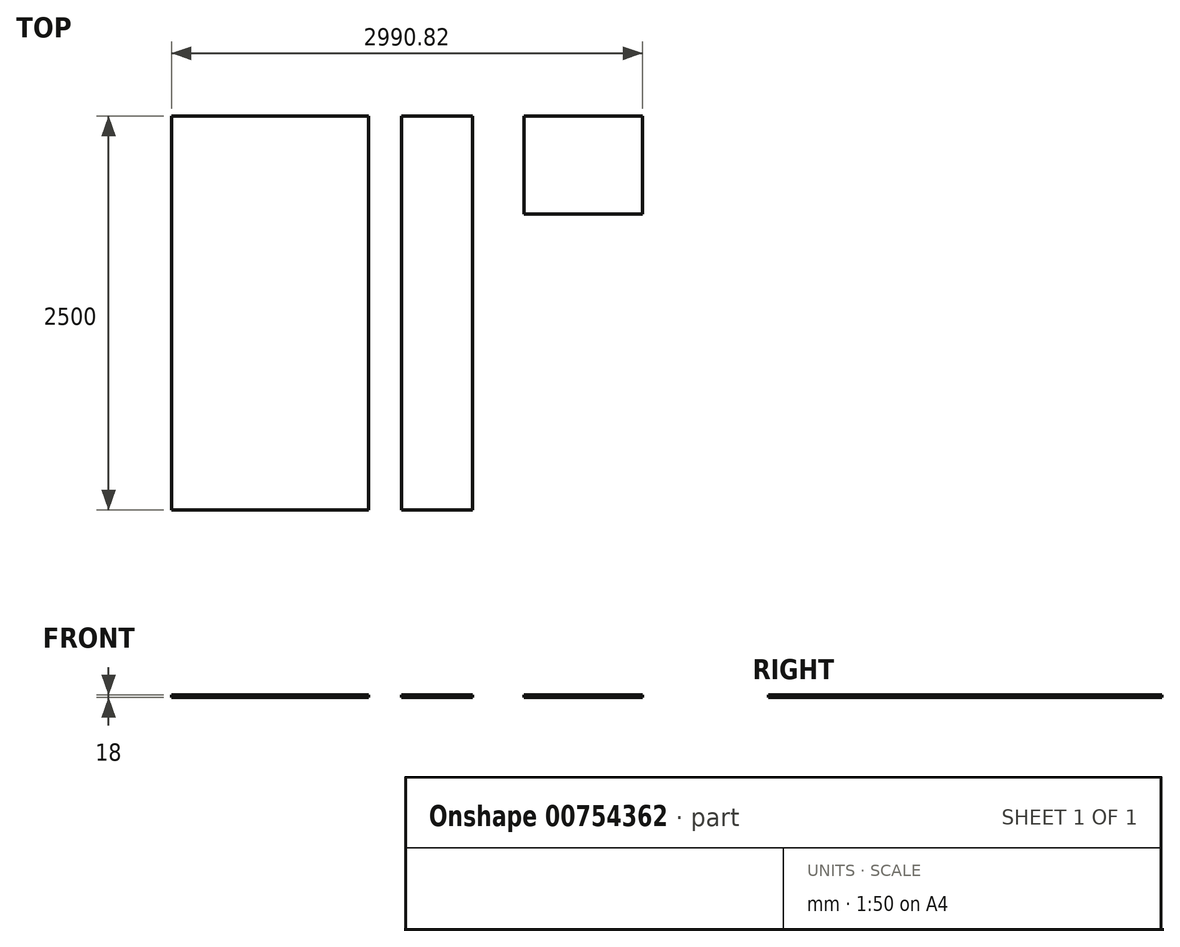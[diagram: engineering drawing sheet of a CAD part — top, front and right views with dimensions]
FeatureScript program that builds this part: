
annotation { "Feature Type Name" : "Feature", "Feature Type Description" : "" }
export const myFeature = defineFeature(function(context is Context, id is Id, definition is map)
    precondition{}
    {
        {
            var Q0;
            Q0=qCreatedBy(makeId("Top.planeOp"),FACE);
            var sketch = newSketch(context, id + "F0", { "sketchPlane" : qUnion([Q0])});
            skLineSegment(sketch, "E0.bottom", {"start": v(0, 0) * mm, "end": v(-1250, 0) * mm});
            skLineSegment(sketch, "E0.top", {"start": v(0, -2500) * mm, "end": v(-1250, -2500) * mm});
            skLineSegment(sketch, "E0.left", {"start": v(0, 0) * mm, "end": v(0, -2500) * mm});
            skLineSegment(sketch, "E0.right", {"start": v(-1250, 0) * mm, "end": v(-1250, -2500) * mm});
            skSolve(sketch);
        }
        {
            var Q0;
            Q0=makeQuery(id+"F0.imprint","IMPRINT",FACE,{"disambiguationData":[TD([[makeQuery(id+"F0.imprint","IMPRINT",EDGE,{"derivedFrom":sQuery(id+"F0.wireOp",EDGE,"E0.bottom")}),1.0]])]});
            extrude(context, id + "F1", {"entities" : qUnion([Q0]), "depth" : 18 * mm, "offsetDistance" : 25 * mm});
        }
        {
            var Q0;
            Q0=qCreatedBy(makeId("Top.planeOp"),FACE);
            var sketch = newSketch(context, id + "F2", { "sketchPlane" : qUnion([Q0])});
            skLineSegment(sketch, "E1.bottom", {"start": v(211.07, 0) * mm, "end": v(660.07, 0) * mm});
            skLineSegment(sketch, "E1.top", {"start": v(211.07, -2500) * mm, "end": v(660.07, -2500) * mm});
            skLineSegment(sketch, "E1.left", {"start": v(211.07, 0) * mm, "end": v(211.07, -2500) * mm});
            skLineSegment(sketch, "E1.right", {"start": v(660.07, 0) * mm, "end": v(660.07, -2500) * mm});
            skSolve(sketch);
        }
        {
            var Q0;
            Q0=makeQuery(id+"F2.imprint","IMPRINT",FACE,{"disambiguationData":[TD([[makeQuery(id+"F2.imprint","IMPRINT",EDGE,{"derivedFrom":sQuery(id+"F2.wireOp",EDGE,"E1.bottom")}),-1.0]])]});
            extrude(context, id + "F3", {"entities" : qUnion([Q0]), "depth" : 18 * mm, "offsetDistance" : 25 * mm});
        }
        {
            var Q0;
            Q0=qCreatedBy(makeId("Top.planeOp"),FACE);
            var sketch = newSketch(context, id + "F4", { "sketchPlane" : qUnion([Q0])});
            skLineSegment(sketch, "E2.bottom", {"start": v(988.32, 0) * mm, "end": v(1740.82, 0) * mm});
            skLineSegment(sketch, "E2.top", {"start": v(988.32, -620) * mm, "end": v(1740.82, -620) * mm});
            skLineSegment(sketch, "E2.left", {"start": v(988.32, 0) * mm, "end": v(988.32, -620) * mm});
            skLineSegment(sketch, "E2.right", {"start": v(1740.82, 0) * mm, "end": v(1740.82, -620) * mm});
            skSolve(sketch);
        }
        {
            var Q0;
            Q0=makeQuery(id+"F4.imprint","IMPRINT",FACE,{"disambiguationData":[TD([[makeQuery(id+"F4.imprint","IMPRINT",EDGE,{"derivedFrom":sQuery(id+"F4.wireOp",EDGE,"E2.bottom")}),-1.0]])]});
            extrude(context, id + "F5", {"entities" : qUnion([Q0]), "depth" : 18 * mm, "offsetDistance" : 25 * mm});
        }
    });
